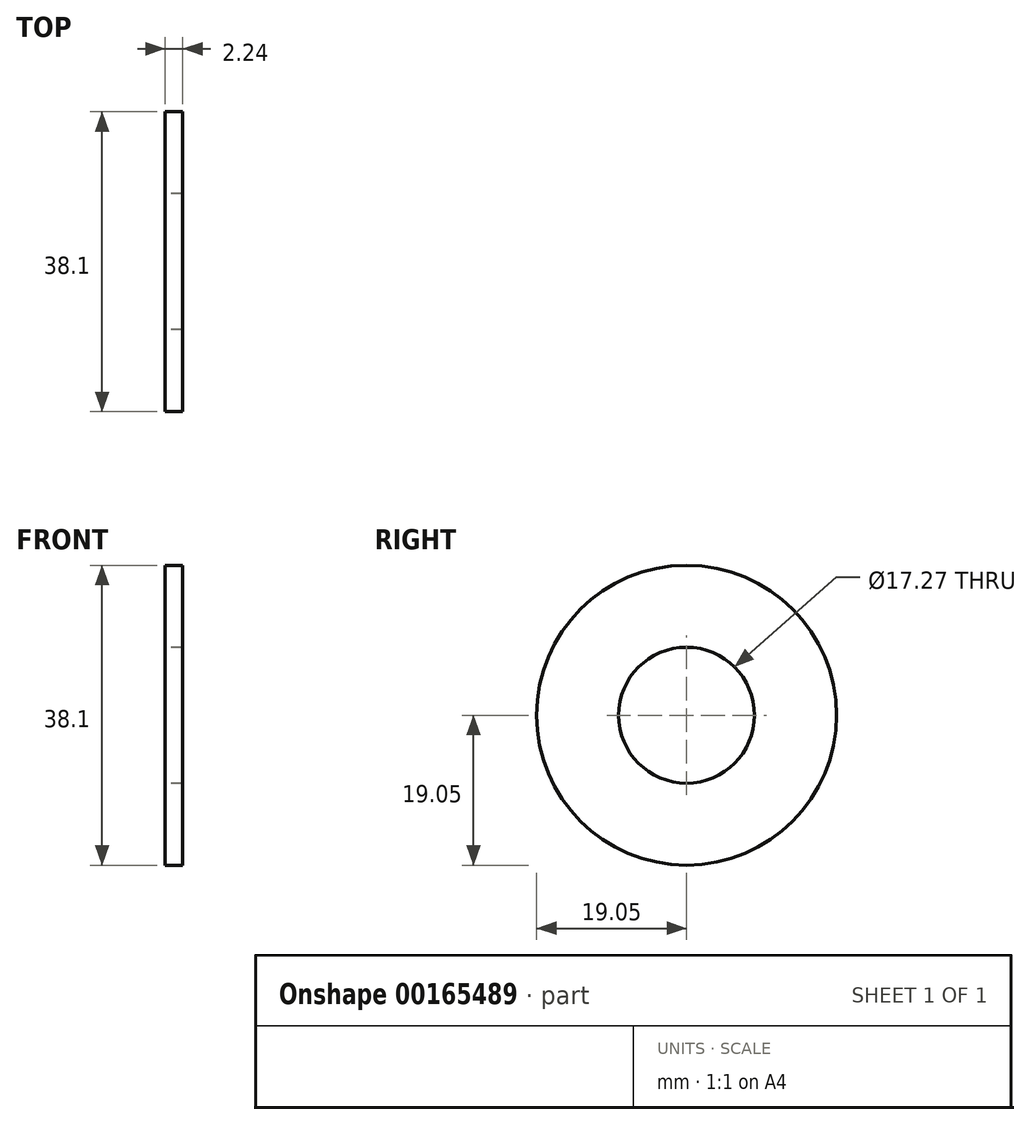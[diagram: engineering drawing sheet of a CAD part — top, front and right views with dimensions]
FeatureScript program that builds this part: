
annotation { "Feature Type Name" : "Feature", "Feature Type Description" : "" }
export const myFeature = defineFeature(function(context is Context, id is Id, definition is map)
    precondition{}
    {
        {
            var Q0;
            Q0=qCreatedBy(makeId("Right.planeOp"),FACE);
            var sketch = newSketch(context, id + "F0", { "sketchPlane" : qUnion([Q0])});
            skCircle(sketch, "E0", {"center": v(0, 0) * mm, "radius": 8.64 * mm});
            skCircle(sketch, "E1", {"center": v(0, 0) * mm, "radius": 19.05 * mm});
            skSolve(sketch);
        }
        {
            var Q0;
            Q0 = qSketchRegion(id + "F0", true);
            extrude(context, id + "F1", {"entities" : qUnion([Q0]), "depth" : 2.24 * mm});
        }
    });
